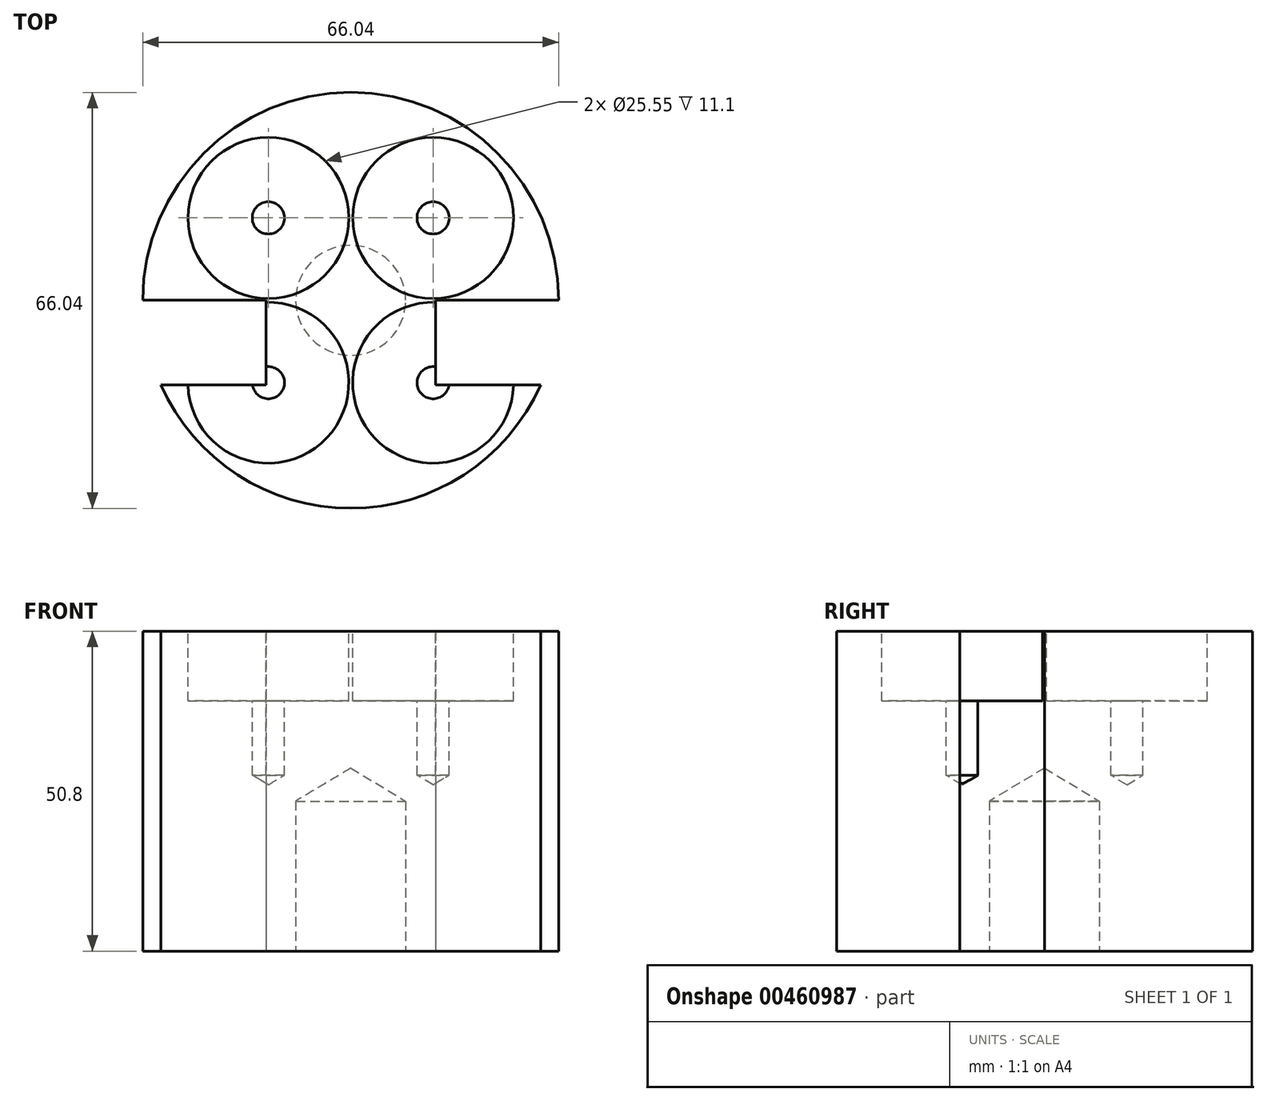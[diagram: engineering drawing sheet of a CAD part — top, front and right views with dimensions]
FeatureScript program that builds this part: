
annotation { "Feature Type Name" : "Feature", "Feature Type Description" : "" }
export const myFeature = defineFeature(function(context is Context, id is Id, definition is map)
    precondition{}
    {
        {
            var Q0;
            Q0=qCreatedBy(makeId("Top.planeOp"),FACE);
            var sketch = newSketch(context, id + "F0", { "sketchPlane" : qUnion([Q0])});
            skCircle(sketch, "E0", {"center": v(-51, 30.81) * mm, "radius": 33.02 * mm});
            skLineSegment(sketch, "E1", {"start": v(-84.02, 30.81) * mm, "end": v(-17.98, 30.81) * mm});
            skLineSegment(sketch, "E2.0", {"start": v(-82.75, 17.35) * mm, "end": v(-19.25, 17.35) * mm});
            skLineSegment(sketch, "E3.0", {"start": v(-82.75, 44.28) * mm, "end": v(-19.25, 44.28) * mm});
            skLineSegment(sketch, "E4", {"start": v(-51, 44.28) * mm, "end": v(-51, 17.35) * mm});
            skLineSegment(sketch, "E5.0", {"start": v(-64.46, 42.75) * mm, "end": v(-64.46, 17.35) * mm});
            skLineSegment(sketch, "E6.0", {"start": v(-37.54, 42.75) * mm, "end": v(-37.54, 17.35) * mm});
            skPoint(sketch, "E7", {"position": v(-64.46, 42.75) * mm});
            skPoint(sketch, "E8", {"position": v(-37.54, 42.75) * mm});
            skPoint(sketch, "E9", {"position": v(-37.54, 17.35) * mm});
            skPoint(sketch, "E10", {"position": v(-64.46, 17.35) * mm});
            skSolve(sketch);
        }
        {
            var Q0;
            Q0=makeQuery(id+"F0.imprint","IMPRINT",FACE,{"disambiguationData":[TD([[makeQuery(id+"F0.imprint","IMPRINT",EDGE,{"derivedFrom":sQuery(id+"F0.wireOp",EDGE,"E0")}),1.0]])]});
            var Q1;
            {var subQ0=sQuery(id+"F0.wireOp",EDGE,"E3.0");var subQ3=sQuery(id+"F0.wireOp",EDGE,"E0");var subQ6=makeQuery(id+"F0.imprint","INTERSECT",VERTEX,{"disambiguationData":[OD(0.0)],"derivedFrom":[subQ3,subQ0]});Q1=makeQuery(id+"F0.imprint","IMPRINT",FACE,{"disambiguationData":[TD([[makeQuery(id+"F0.imprint","IMPRINT",EDGE,{"disambiguationData":[TD([[subQ6,-1.0]])],"derivedFrom":subQ3}),1.0]])]});}
            var Q2;
            {var subQ0=sQuery(id+"F0.wireOp",EDGE,"E2.0");var subQ4=sQuery(id+"F0.wireOp",EDGE,"E0");var subQ5=makeQuery(id+"F0.imprint","INTERSECT",VERTEX,{"disambiguationData":[OD(0.0)],"derivedFrom":[subQ4,subQ0]});Q2=makeQuery(id+"F0.imprint","IMPRINT",FACE,{"disambiguationData":[TD([[makeQuery(id+"F0.imprint","IMPRINT",EDGE,{"disambiguationData":[TD([[subQ5,-1.0]])],"derivedFrom":subQ4}),1.0]])]});}
            var Q3;
            {var subQ0=sQuery(id+"F0.wireOp",EDGE,"E5.0");var subQ1=sQuery(id+"F0.wireOp",EDGE,"E1");var subQ2=makeQuery(id+"F0.imprint","INTERSECT",VERTEX,{"derivedFrom":[subQ1,subQ0]});Q3=makeQuery(id+"F0.imprint","IMPRINT",FACE,{"disambiguationData":[TD([[makeQuery(id+"F0.imprint","IMPRINT",EDGE,{"disambiguationData":[TD([[subQ2,-1.0]])],"derivedFrom":subQ1}),-1.0]])]});}
            var Q4;
            {var subQ0=sQuery(id+"F0.wireOp",EDGE,"E4");var subQ1=sQuery(id+"F0.wireOp",EDGE,"E1");var subQ2=makeQuery(id+"F0.imprint","INTERSECT",VERTEX,{"derivedFrom":[subQ1,subQ0]});Q4=makeQuery(id+"F0.imprint","IMPRINT",FACE,{"disambiguationData":[TD([[makeQuery(id+"F0.imprint","IMPRINT",EDGE,{"disambiguationData":[TD([[subQ2,-1.0]])],"derivedFrom":subQ1}),-1.0]])]});}
            var Q5;
            {var subQ0=sQuery(id+"F0.wireOp",EDGE,"E4");var subQ1=sQuery(id+"F0.wireOp",EDGE,"E1");var subQ2=makeQuery(id+"F0.imprint","INTERSECT",VERTEX,{"derivedFrom":[subQ1,subQ0]});Q5=makeQuery(id+"F0.imprint","IMPRINT",FACE,{"disambiguationData":[TD([[makeQuery(id+"F0.imprint","IMPRINT",EDGE,{"disambiguationData":[TD([[subQ2,-1.0]])],"derivedFrom":subQ1}),1.0]])]});}
            var Q6;
            {var subQ0=sQuery(id+"F0.wireOp",EDGE,"E5.0");var subQ1=sQuery(id+"F0.wireOp",EDGE,"E1");var subQ2=makeQuery(id+"F0.imprint","INTERSECT",VERTEX,{"derivedFrom":[subQ1,subQ0]});Q6=makeQuery(id+"F0.imprint","IMPRINT",FACE,{"disambiguationData":[TD([[makeQuery(id+"F0.imprint","IMPRINT",EDGE,{"disambiguationData":[TD([[subQ2,-1.0]])],"derivedFrom":subQ1}),1.0]])]});}
            var Q7;
            {var subQ0=sQuery(id+"F0.wireOp",EDGE,"E1");var subQ1=sQuery(id+"F0.wireOp",EDGE,"E0");var subQ2=makeQuery(id+"F0.imprint","INTERSECT",VERTEX,{"disambiguationData":[OD(0.0)],"derivedFrom":[subQ1,subQ0]});Q7=makeQuery(id+"F0.imprint","IMPRINT",FACE,{"disambiguationData":[TD([[makeQuery(id+"F0.imprint","IMPRINT",EDGE,{"disambiguationData":[TD([[subQ2,-1.0]])],"derivedFrom":subQ1}),1.0]])]});}
            var Q8;
            {var subQ0=sQuery(id+"F0.wireOp",EDGE,"E1");var subQ1=sQuery(id+"F0.wireOp",EDGE,"E0");var subQ2=makeQuery(id+"F0.imprint","INTERSECT",VERTEX,{"disambiguationData":[OD(1.0)],"derivedFrom":[subQ1,subQ0]});Q8=makeQuery(id+"F0.imprint","IMPRINT",FACE,{"disambiguationData":[TD([[makeQuery(id+"F0.imprint","IMPRINT",EDGE,{"disambiguationData":[TD([[subQ2,1.0]])],"derivedFrom":subQ1}),1.0]])]});}
            extrude(context, id + "F1", {"entities" : qUnion([Q0, Q1, Q2, Q3, Q4, Q5, Q6, Q7, Q8]), "depth" : 50.8 * mm, "offsetDistance" : 25.4 * mm});
        }
        {
            var Q0;
            Q0=makeQuery(id+"F1.opExtrude","CAP_FACE",FACE,{"disambiguationData":[OSD([sQuery(id+"F0.wireOp",EDGE,"E0")])],"isStart":false});
            var sketch = newSketch(context, id + "F2", { "sketchPlane" : qUnion([Q0])});
            skPoint(sketch, "E11", {"position": v(-51, 30.81) * mm});
            skSolve(sketch);
        }
        {
            var Q0;
            Q0=makeQuery(id+"F1.opExtrude","CAP_FACE",FACE,{"disambiguationData":[OSD([sQuery(id+"F0.wireOp",EDGE,"E0")])],"isStart":true});
            var sketch = newSketch(context, id + "F3", { "sketchPlane" : qUnion([Q0])});
            skPoint(sketch, "E12", {"position": v(-51, -30.81) * mm});
            skSolve(sketch);
        }
        {
            var Q0;
            Q0=makeQuery(id+"F2.imprint","IMPRINT",FACE,{"disambiguationData":[TD([[makeQuery(id+"F2.imprint","IMPRINT",EDGE,{"derivedFrom":makeQuery(id+"F1.opExtrude","CAP_EDGE",EDGE,{"disambiguationData":[OSD([sQuery(id+"F0.wireOp",EDGE,"E0")])],"isStart":false})}),1.0]])]});
            var sketch = newSketch(context, id + "F4", { "sketchPlane" : qUnion([Q0])});
            skPoint(sketch, "E13", {"position": v(-64.08, 43.9) * mm});
            skPoint(sketch, "E14", {"position": v(-37.92, 43.9) * mm});
            skPoint(sketch, "E15", {"position": v(-37.92, 17.73) * mm});
            skPoint(sketch, "E16", {"position": v(-64.08, 17.73) * mm});
            skSolve(sketch);
        }
        {
            var Q0;
            Q0=sQuery(id+"F4.wireOp",VERTEX,"E13");
            var Q1;
            Q1=sQuery(id+"F4.wireOp",VERTEX,"E14");
            var Q2;
            Q2=sQuery(id+"F4.wireOp",VERTEX,"E15");
            var Q3;
            Q3=sQuery(id+"F4.wireOp",VERTEX,"E16");
            var Q4;
            Q4=makeQuery(id+"F1.opExtrude","SWEPT_BODY",BODY,{"disambiguationData":[OSD([sQuery(id+"F0.wireOp",EDGE,"E0")])]});
            hole(context, id + "F5", {"style" : HoleStyle.C_BORE, "endStyle" : HoleEndStyle.BLIND, "holeDiameter" : 5.1 * mm, "cBoreDiameter" : 25.55 * mm, "cBoreDepth" : 11.1 * mm, "majorDiameter" : 6.35 * mm, "holeDepth" : 22.86 * mm, "isTappedThrough" : true, "tappedDepth" : 19.05 * mm, "tapClearance" : 3, "locations" : qUnion([Q0, Q1, Q2, Q3]), "scope" : qUnion([Q4])});
        }
        {
            var Q0;
            Q0=sQuery(id+"F3.wireOp",VERTEX,"E12");
            var Q1;
            Q1=makeQuery(id+"F1.opExtrude","SWEPT_BODY",BODY,{"disambiguationData":[OSD([sQuery(id+"F0.wireOp",EDGE,"E0")])]});
            hole(context, id + "F6", {"style" : HoleStyle.SIMPLE, "endStyle" : HoleEndStyle.BLIND, "standardTappedOrClearance" : lookupTablePath({ "standard" : "ANSI", "engagement" : "75%", "pitch" : "16 tpi", "size" : "3/4", "type" : "Tapped" }), "standardBlindInLast" : lookupTablePath({ "standard" : "ANSI", "engagement" : "75%", "pitch" : "16 tpi", "size" : "3/4", "type" : "Tapped" }), "holeDiameter" : 17.46 * mm, "majorDiameter" : 19.05 * mm, "showTappedDepth" : true, "holeDepth" : 23.8 * mm, "isTappedThrough" : true, "tappedDepth" : 19.05 * mm, "tapClearance" : 3, "locations" : qUnion([Q0]), "scope" : qUnion([Q1])});
        }
    });
